annotation { "Feature Type Name" : "Feature", "Feature Type Description" : "" }
export const myFeature = defineFeature(function(context is Context, id is Id, definition is map)
    precondition{}
    {
        {
            var Q0;
            Q0=qCreatedBy(makeId("Front.planeOp"),FACE);
            var sketch = newSketch(context, id + "F0", { "sketchPlane" : qUnion([Q0])});
            skFitSpline(sketch, "E0", {"points": [v(-54.75, 32.97) * mm, v(-60.47, 11.9) * mm, v(-61.53, -25.48) * mm, v(-85.3, -40.51) * mm, v(-53.1, -42.47) * mm, v(-32.84, -50.72) * mm, v(-23.34, -52.1) * mm, v(-12.15, -51.73) * mm, v(0, -46.96) * mm, v(-25.25, -43.36) * mm, v(-46.55, -35.14) * mm, v(-51.34, -23.34) * mm, v(-53.34, -7.1) * mm, v(-51.02, 19.95) * mm, v(-25.01, 39.76) * mm, v(-41.19, 36.16) * mm, v(-54.75, 32.97) * mm]});
            skLineSegment(sketch, "E1", {"start": v(0, 75.72) * mm, "end": v(0, -68.16) * mm});
            skSolve(sketch);
        }
        {
            var Q0;
            {var subQ0=sQuery(id+"F0.wireOp",EDGE,"E1");var subQ1=sQuery(id+"F0.wireOp",EDGE,"E0");var subQ2=makeQuery(id+"F0.imprint","INTERSECT",VERTEX,{"disambiguationData":[OD(0.0)],"derivedFrom":[subQ1,subQ0]});Q0=makeQuery(id+"F0.imprint","IMPRINT",FACE,{"disambiguationData":[TD([[makeQuery(id+"F0.imprint","IMPRINT",EDGE,{"disambiguationData":[TD([[subQ2,1.0]])],"derivedFrom":subQ1}),1.0]])]});}
            var Q1;
            Q1=sQuery(id+"F0.wireOp",EDGE,"E1");
            revolve(context, id + "F1", {"surfaceOperationType" : NewSurfaceOperationType.NEW, "entities" : qUnion([Q0]), "axis" : qUnion([Q1]), "revolveType" : RevolveType.FULL});
        }
    });